# Revit family: STL22461BR_30_40_STL22461PTO_30_40
name_source: partatom
category: Luminárias
units: mm (PartAtom-declared; Revit-internal decimal feet)

## family parameters
Com base no plano de trabalho = Não
Compartilhado = Não
Corte com vazios quando carregada = Não
Cota do conector redondo = Utilizar diâmetro
Fonte luminosa = Sim
Manter orientação da anotação = Não
Ponto de cálculo do ambiente = Não
Sempre na vertical = Sim
Tipo de parte = Normal

## types (4) — shared parameters
Altura = 0.05 m
Comprimento = 0.59 m
Dimerização = Não dimerizável
Fabricante = Stella
Filtro de cor = 16777215
Grau de proteção (IP) = IP20
IRC (Índice de reprodução de cores) = >93 (R9>60)
Largura = 0.04 m
Modelo = Trace
Potência máxima = 25 W
Tensão Elétrica = 100V-240V
Troca de temperatura da cor de lâmpada com esmaecimento = <Nenhum>
URL = https://stella.com.br
Ângulo de Abertura = 80°
Ângulo de inclinação = 90.00°
zero-valued in all types: Elevação padrão

## per-type parameters (varying)
| type | Arquivo de rede fotométrica | Estrutura | Fluxo Luminoso | Luminoso | Parafuso Branco | Parafuso Preto | Referência | Temperatura da cor (K) |
| STL22461BR/30 - BIVOLT - 3000K - 1400lm - 80° | STELLA - STL22461BR-30 - TRACE 25W - LUMINÁRIA DE LUZ GERAL.ies | Al - Branco | 1400 lm | Luminoso - 3000K | Sim | Não | STL22461BR/30 - BIVOLT | 3000 K |
| STL22461BR/40 - BIVOLT - 4000K - 1450lm - 80° | STELLA - STL22461BR-40 - TRACE 25W - LUMINÁRIA DE LUZ GERAL.ies | Al - Branco | 1450 lm | Luminoso - 4000K | Sim | Não | STL22461BR/40 - BIVOLT | 4000 K |
| STL22461PTO/30 - BIVOLT - 3000K - 900lm - 80° | STELLA - STL22461PTO-30 - TRACE 25W - LUMINÁRIA DE LUZ GERAL.ies | Al - Preto | 900 lm | Luminoso - 3000K | Não | Sim | STL22461PTO/30 - BIVOLT | 3000 K |
| STL22461PTO/40 - BIVOLT - 4000K - 950lm - 80° | STELLA - STL22461PTO-40 - TRACE 25W - LUMINÁRIA DE LUZ GERAL.ies | Al - Preto | 950 lm | Luminoso - 4000K | Não | Sim | STL22461PTO/40 - BIVOLT | 4000 K |
